# Revit family: MARK Product_ Studioscape_ Table Family
name_source: partatom
category: Furniture
revit_build: Autodesk Revit 2018 (Build: 20170223_1515(x64)
units: mm (PartAtom-declared; Revit-internal decimal feet)

## family parameters
Always vertical = Yes
Cut with Voids When Loaded = No
OmniClass Number = 23.40.20.00
OmniClass Title = General Furniture and Specialties
Room Calculation Point = No
Shared = No
Work Plane-Based = No

## types (3) — shared parameters
FabricMaterial = Fabric (Signal Red)
Manufacturer = MARK Product
SledMaterial = Powder Coat (Tele Grey)
Surface Material = Oak
URL = http://www.markproduct.com

## per-type parameters (varying)
| type | Furniture Type |
| Coffee Table (750X750X200) | StudioCoffeeTable : Coffee Table |
| Coffee Table (750X750X390) | StudioCoffeeTable : Medium coffee Table |
| High Table/Armrest (750X375X650) | StudioCoffeeTable : High Table/Armrest |

## geometry (parser evidence)
native form markers: Sweep x85
no freeform markers — native parametric forms only
